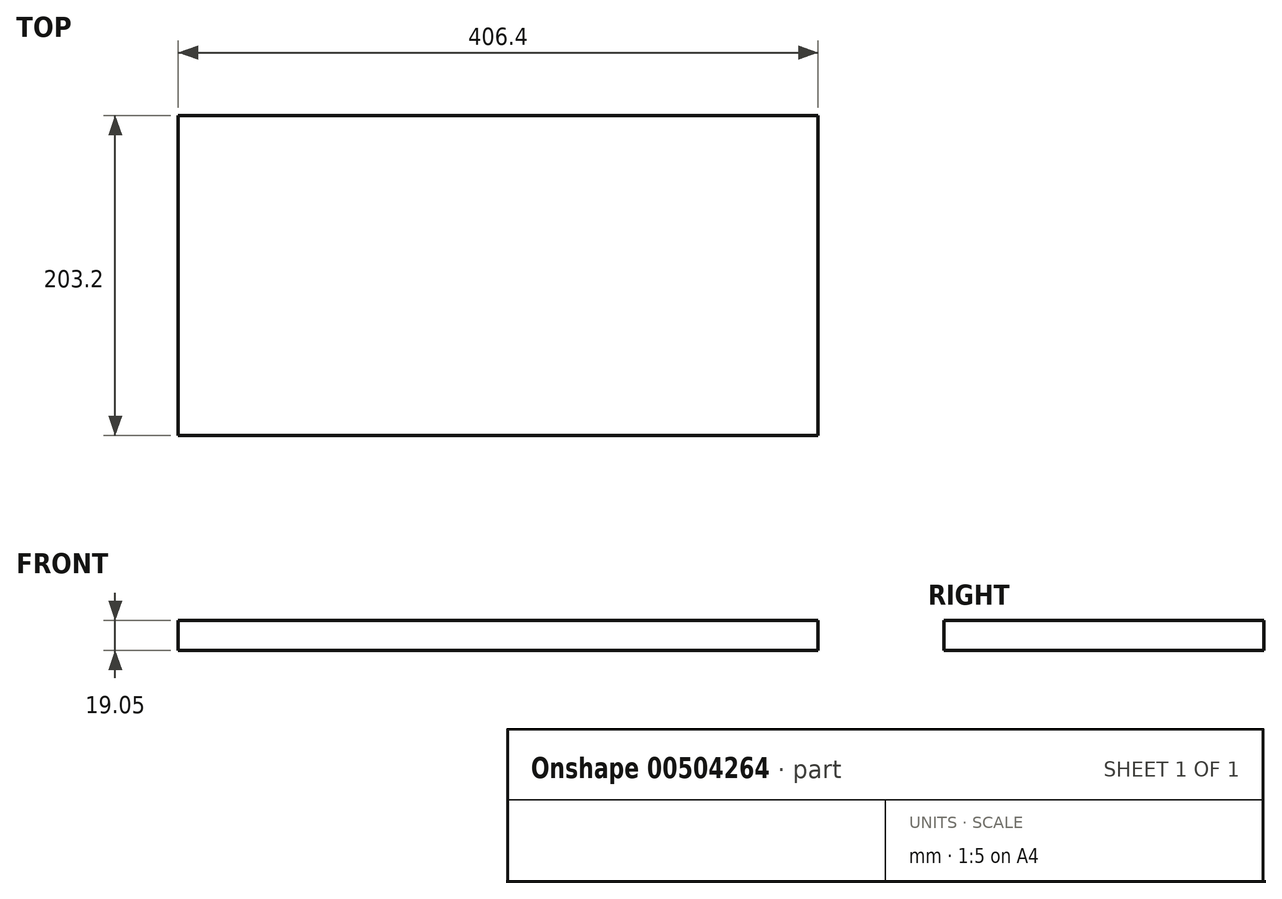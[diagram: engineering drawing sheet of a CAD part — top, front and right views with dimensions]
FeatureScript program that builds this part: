
annotation { "Feature Type Name" : "Feature", "Feature Type Description" : "" }
export const myFeature = defineFeature(function(context is Context, id is Id, definition is map)
    precondition{}
    {
        {
            var Q0;
            Q0=qCreatedBy(makeId("Top.planeOp"),FACE);
            var sketch = newSketch(context, id + "F0", { "sketchPlane" : qUnion([Q0])});
            skLineSegment(sketch, "E0.bottom", {"start": v(203.2, -101.6) * mm, "end": v(-203.2, -101.6) * mm});
            skLineSegment(sketch, "E0.top", {"start": v(203.2, 101.6) * mm, "end": v(-203.2, 101.6) * mm});
            skLineSegment(sketch, "E0.left", {"start": v(203.2, -101.6) * mm, "end": v(203.2, 101.6) * mm});
            skLineSegment(sketch, "E0.right", {"start": v(-203.2, -101.6) * mm, "end": v(-203.2, 101.6) * mm});
            skPoint(sketch, "E0.middle", {"position": v(0, 0) * mm});
            skSolve(sketch);
        }
        {
            var Q0;
            Q0=makeQuery(id+"F0.imprint","IMPRINT",FACE,{"disambiguationData":[TD([[makeQuery(id+"F0.imprint","IMPRINT",EDGE,{"derivedFrom":sQuery(id+"F0.wireOp",EDGE,"E0.bottom")}),-1.0]])]});
            extrude(context, id + "F1", {"entities" : qUnion([Q0]), "depth" : 19.05 * mm});
        }
    });
